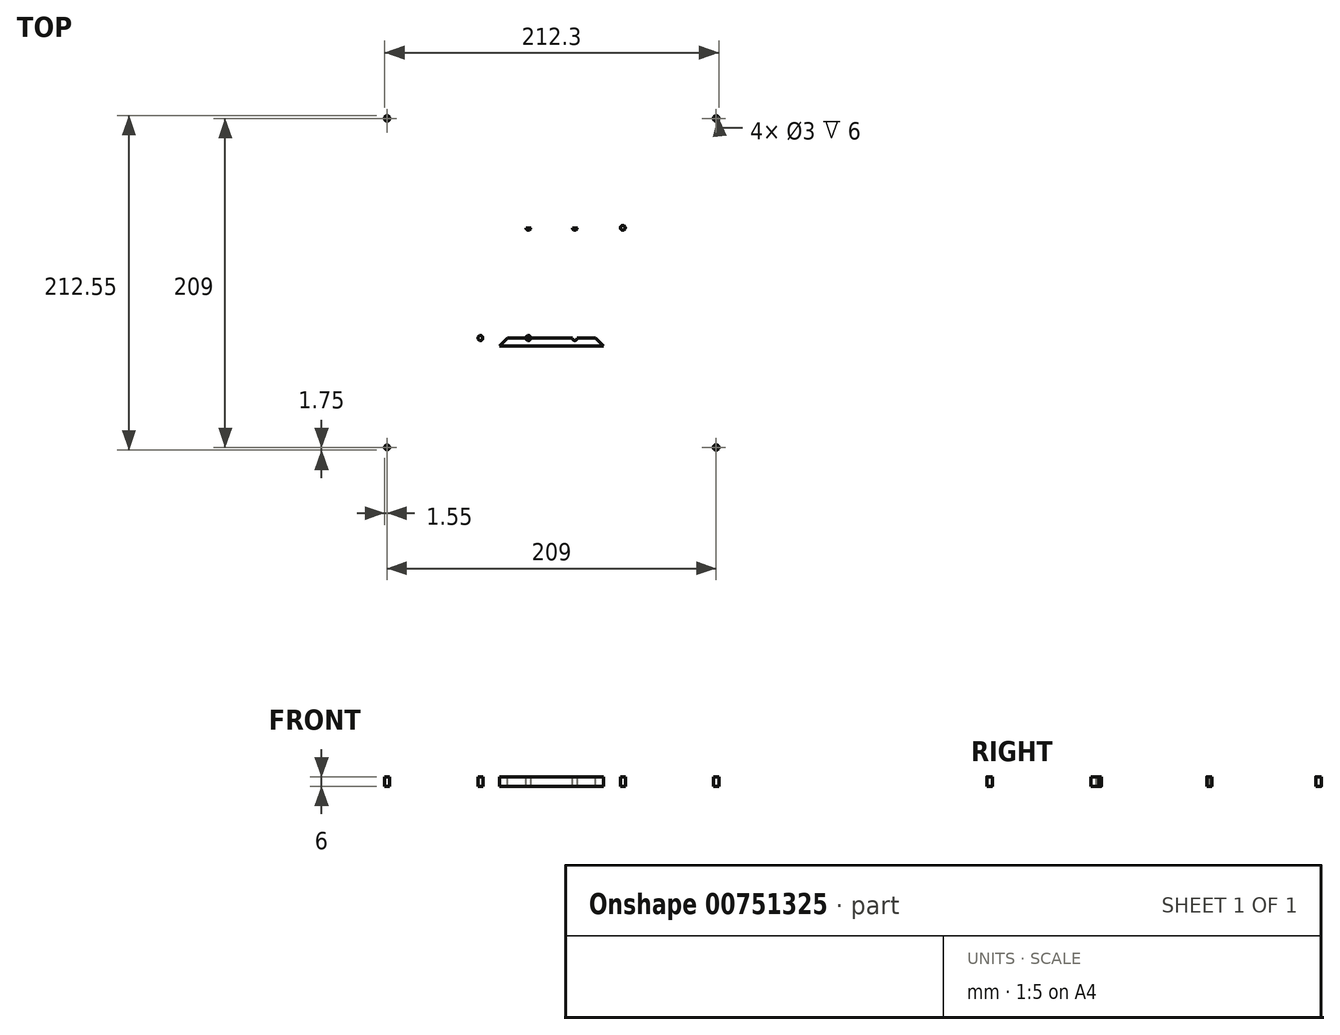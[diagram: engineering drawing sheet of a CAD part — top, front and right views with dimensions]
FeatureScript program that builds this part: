
annotation { "Feature Type Name" : "Feature", "Feature Type Description" : "" }
export const myFeature = defineFeature(function(context is Context, id is Id, definition is map)
    precondition{}
    {
        {
            var Q0;
            Q0=qCreatedBy(makeId("Top.planeOp"),FACE);
            var sketch = newSketch(context, id + "F0", { "sketchPlane" : qUnion([Q0])});
            skLineSegment(sketch, "E0", {"start": v(-180, -185) * mm, "end": v(-185, -180.2) * mm});
            skLineSegment(sketch, "E1", {"start": v(-185, -180.2) * mm, "end": v(-185, 180) * mm});
            skLineSegment(sketch, "E2", {"start": v(-185, 180) * mm, "end": v(-180, 185) * mm});
            skLineSegment(sketch, "E3", {"start": v(-180, 185) * mm, "end": v(180, 185) * mm});
            skLineSegment(sketch, "E4", {"start": v(180, 185) * mm, "end": v(185, 180) * mm});
            skLineSegment(sketch, "E5", {"start": v(185, 180) * mm, "end": v(185, -180) * mm});
            skLineSegment(sketch, "E6", {"start": v(185, -180) * mm, "end": v(180, -185) * mm});
            skLineSegment(sketch, "E7", {"start": v(180, -185) * mm, "end": v(160, -185) * mm});
            skLineSegment(sketch, "E8", {"start": v(160, -185) * mm, "end": v(158, -183) * mm});
            skLineSegment(sketch, "E9", {"start": v(144, -183) * mm, "end": v(-144, -183) * mm});
            skLineSegment(sketch, "E10", {"start": v(-158, -183) * mm, "end": v(-160, -185) * mm});
            skLineSegment(sketch, "E11", {"start": v(-160, -185) * mm, "end": v(-180, -185) * mm});
            skArc(sketch, "E12", {"start": v(-90, -165) * mm, "mid": v(-85, -170) * mm, "end": v(-80, -165) * mm});
            skLineSegment(sketch, "E13", {"start": v(-90, -165) * mm, "end": v(-90, -150) * mm});
            skLineSegment(sketch, "E14", {"start": v(-90, -150) * mm, "end": v(-105, -135) * mm});
            skLineSegment(sketch, "E15", {"start": v(-105, -135) * mm, "end": v(-125, -135) * mm});
            skLineSegment(sketch, "E16", {"start": v(-125, -135) * mm, "end": v(-130, -130) * mm});
            skLineSegment(sketch, "E17", {"start": v(-130, -130) * mm, "end": v(-130, 140) * mm});
            skLineSegment(sketch, "E18", {"start": v(-130, 140) * mm, "end": v(-125, 145) * mm});
            skLineSegment(sketch, "E19", {"start": v(-125, 145) * mm, "end": v(125, 145) * mm});
            skLineSegment(sketch, "E20", {"start": v(125, 145) * mm, "end": v(130, 140) * mm});
            skLineSegment(sketch, "E21", {"start": v(130, 140) * mm, "end": v(130, -130) * mm});
            skLineSegment(sketch, "E22", {"start": v(130, -130) * mm, "end": v(125, -135) * mm});
            skLineSegment(sketch, "E23", {"start": v(-80, -165) * mm, "end": v(-80, -150) * mm});
            skLineSegment(sketch, "E24", {"start": v(-80, -150) * mm, "end": v(-75, -145) * mm});
            skArc(sketch, "E25", {"start": v(80, -165) * mm, "mid": v(85, -170) * mm, "end": v(90, -165) * mm});
            skLineSegment(sketch, "E26", {"start": v(125, -135) * mm, "end": v(105, -135) * mm});
            skLineSegment(sketch, "E27", {"start": v(106, -134) * mm, "end": v(90, -150) * mm});
            skLineSegment(sketch, "E28", {"start": v(90, -150) * mm, "end": v(90, -165) * mm});
            skLineSegment(sketch, "E29", {"start": v(80, -165) * mm, "end": v(80, -150) * mm});
            skLineSegment(sketch, "E30", {"start": v(80, -150) * mm, "end": v(75, -145) * mm});
            skLineSegment(sketch, "E31", {"start": v(-5, -170) * mm, "end": v(5, -170) * mm});
            skLineSegment(sketch, "E32", {"start": v(5, -170) * mm, "end": v(30, -145) * mm});
            skLineSegment(sketch, "E33", {"start": v(-5, -170) * mm, "end": v(-30, -145) * mm});
            skLineSegment(sketch, "E34", {"start": v(-75, -145) * mm, "end": v(-30, -145) * mm});
            skLineSegment(sketch, "E35", {"start": v(30, -145) * mm, "end": v(75, -145) * mm});
            skLineSegment(sketch, "E36", {"start": v(-120, 140) * mm, "end": v(-122, 140) * mm});
            skLineSegment(sketch, "E37", {"start": v(-122, 140) * mm, "end": v(-125, 137) * mm});
            skLineSegment(sketch, "E38", {"start": v(-125, 137) * mm, "end": v(-125, 135) * mm});
            skLineSegment(sketch, "E39", {"start": v(-125, 135) * mm, "end": v(-125, 133) * mm});
            skLineSegment(sketch, "E40", {"start": v(-125, 133) * mm, "end": v(-105, 113) * mm});
            skLineSegment(sketch, "E41", {"start": v(-105, 113) * mm, "end": v(-105, 93) * mm});
            skLineSegment(sketch, "E42", {"start": v(-105, 93) * mm, "end": v(-115, 83) * mm});
            skLineSegment(sketch, "E43", {"start": v(-115, -23) * mm, "end": v(-105, -33) * mm});
            skLineSegment(sketch, "E44", {"start": v(-125, -73) * mm, "end": v(-105, -53) * mm});
            skLineSegment(sketch, "E45", {"start": v(-105, -53) * mm, "end": v(-105, -33) * mm});
            skLineSegment(sketch, "E46", {"start": v(-125, -73) * mm, "end": v(-125, -77) * mm});
            skLineSegment(sketch, "E47", {"start": v(-125, -77) * mm, "end": v(-122, -80) * mm});
            skLineSegment(sketch, "E48", {"start": v(-122, -80) * mm, "end": v(-120, -80) * mm});
            skLineSegment(sketch, "E49", {"start": v(90, -80) * mm, "end": v(92, -80) * mm});
            skLineSegment(sketch, "E50", {"start": v(92, -80) * mm, "end": v(95, -77) * mm});
            skLineSegment(sketch, "E51", {"start": v(95, 136) * mm, "end": v(95, 137) * mm});
            skLineSegment(sketch, "E52", {"start": v(95, 137) * mm, "end": v(92, 140) * mm});
            skLineSegment(sketch, "E53", {"start": v(95, 133) * mm, "end": v(55, 93) * mm});
            skLineSegment(sketch, "E54", {"start": v(85, 43) * mm, "end": v(75, 53) * mm});
            skLineSegment(sketch, "E55", {"start": v(75, 53) * mm, "end": v(55, 73) * mm});
            skLineSegment(sketch, "E56", {"start": v(55, 73) * mm, "end": v(55, 93) * mm});
            skLineSegment(sketch, "E57", {"start": v(85, 17) * mm, "end": v(75, 7) * mm});
            skLineSegment(sketch, "E58", {"start": v(75, 7) * mm, "end": v(55, -13) * mm});
            skLineSegment(sketch, "E59", {"start": v(95, -73) * mm, "end": v(75, -53) * mm});
            skLineSegment(sketch, "E60", {"start": v(75, -53) * mm, "end": v(55, -33) * mm});
            skLineSegment(sketch, "E61", {"start": v(55, -33) * mm, "end": v(55, -13) * mm});
            skLineSegment(sketch, "E62", {"start": v(88, 140) * mm, "end": v(65, 117) * mm});
            skLineSegment(sketch, "E63", {"start": v(25, 77) * mm, "end": v(23, 75) * mm});
            skLineSegment(sketch, "E64", {"start": v(23, 75) * mm, "end": v(13, 65) * mm});
            skLineSegment(sketch, "E65", {"start": v(13, 65) * mm, "end": v(-43, 65) * mm});
            skLineSegment(sketch, "E66", {"start": v(88, -80) * mm, "end": v(63, -55) * mm});
            skLineSegment(sketch, "E67", {"start": v(13, -5) * mm, "end": v(-43, -5) * mm});
            skLineSegment(sketch, "E68", {"start": v(-93, 115) * mm, "end": v(63, 115) * mm});
            skLineSegment(sketch, "E69", {"start": v(-93, -55) * mm, "end": v(63, -55) * mm});
            skLineSegment(sketch, "E70", {"start": v(-115, 45) * mm, "end": v(-105, 35) * mm});
            skLineSegment(sketch, "E71", {"start": v(-105, 35) * mm, "end": v(-105, 25) * mm});
            skLineSegment(sketch, "E72", {"start": v(-105, 25) * mm, "end": v(-115, 15) * mm});
            skLineSegment(sketch, "E73", {"start": v(-95, 35) * mm, "end": v(-75, 55) * mm});
            skLineSegment(sketch, "E74", {"start": v(-75, 55) * mm, "end": v(-55, 55) * mm});
            skLineSegment(sketch, "E75", {"start": v(-55, 55) * mm, "end": v(-35, 35) * mm});
            skLineSegment(sketch, "E76", {"start": v(-35, 35) * mm, "end": v(-35, 25) * mm});
            skLineSegment(sketch, "E77", {"start": v(-35, 25) * mm, "end": v(-55, 5) * mm});
            skLineSegment(sketch, "E78", {"start": v(-55, 5) * mm, "end": v(-75, 5) * mm});
            skLineSegment(sketch, "E79", {"start": v(-75, 5) * mm, "end": v(-95, 25) * mm});
            skLineSegment(sketch, "E80", {"start": v(-95, 25) * mm, "end": v(-95, 35) * mm});
            skLineSegment(sketch, "E81", {"start": v(35, 55) * mm, "end": v(55, 35) * mm});
            skLineSegment(sketch, "E82", {"start": v(55, 35) * mm, "end": v(55, 25) * mm});
            skLineSegment(sketch, "E83", {"start": v(55, 25) * mm, "end": v(35, 5) * mm});
            skLineSegment(sketch, "E84", {"start": v(35, 5) * mm, "end": v(25, 5) * mm});
            skLineSegment(sketch, "E85", {"start": v(25, 5) * mm, "end": v(5, 25) * mm});
            skLineSegment(sketch, "E86", {"start": v(5, 25) * mm, "end": v(5, 35) * mm});
            skLineSegment(sketch, "E87", {"start": v(5, 35) * mm, "end": v(25, 55) * mm});
            skLineSegment(sketch, "E88", {"start": v(25, 55) * mm, "end": v(35, 55) * mm});
            skLineSegment(sketch, "E89", {"start": v(-120, 140) * mm, "end": v(-118, 140) * mm});
            skLineSegment(sketch, "E90", {"start": v(92, 140) * mm, "end": v(88, 140) * mm});
            skLineSegment(sketch, "E91", {"start": v(95, 136) * mm, "end": v(95, 133) * mm});
            skLineSegment(sketch, "E92", {"start": v(95, -73) * mm, "end": v(95, -77) * mm});
            skLineSegment(sketch, "E93", {"start": v(88, -80) * mm, "end": v(90, -80) * mm});
            skLineSegment(sketch, "E94", {"start": v(-118, -80) * mm, "end": v(-120, -80) * mm});
            skLineSegment(sketch, "E95", {"start": v(-83, 105) * mm, "end": v(53, 105) * mm});
            skLineSegment(sketch, "E96", {"start": v(65, 117) * mm, "end": v(63, 115) * mm});
            skLineSegment(sketch, "E97", {"start": v(53, 105) * mm, "end": v(25, 77) * mm});
            skLineSegment(sketch, "E98", {"start": v(-118, 140) * mm, "end": v(-93, 115) * mm});
            skLineSegment(sketch, "E99", {"start": v(-83, 105) * mm, "end": v(-43, 65) * mm});
            skLineSegment(sketch, "E100", {"start": v(53, -45) * mm, "end": v(-83, -45) * mm});
            skLineSegment(sketch, "E101", {"start": v(-118, -80) * mm, "end": v(-93, -55) * mm});
            skLineSegment(sketch, "E102", {"start": v(-43, -5) * mm, "end": v(-83, -45) * mm});
            skLineSegment(sketch, "E103", {"start": v(13, -5) * mm, "end": v(53, -45) * mm});
            skLineSegment(sketch, "E104", {"start": v(-127.97, 156.16) * mm, "end": v(-127.9, 173.41) * mm});
            skLineSegment(sketch, "E105", {"start": v(-127.9, 173.41) * mm, "end": v(-120.91, 173.41) * mm});
            skLineSegment(sketch, "E106", {"start": v(-120.91, 173.41) * mm, "end": v(-118.76, 172.76) * mm});
            skLineSegment(sketch, "E107", {"start": v(-118.76, 172.76) * mm, "end": v(-117.71, 171.78) * mm});
            skLineSegment(sketch, "E108", {"start": v(-117.71, 171.78) * mm, "end": v(-117, 170.47) * mm});
            skLineSegment(sketch, "E109", {"start": v(-117, 170.47) * mm, "end": v(-116.67, 168.7) * mm});
            skLineSegment(sketch, "E110", {"start": v(-116.67, 168.7) * mm, "end": v(-117, 167) * mm});
            skLineSegment(sketch, "E111", {"start": v(-117, 167) * mm, "end": v(-117.84, 165.57) * mm});
            skLineSegment(sketch, "E112", {"start": v(-117.84, 165.57) * mm, "end": v(-119.02, 164.85) * mm});
            skLineSegment(sketch, "E113", {"start": v(-119.02, 164.85) * mm, "end": v(-120.2, 164.52) * mm});
            skLineSegment(sketch, "E114", {"start": v(-120.2, 164.52) * mm, "end": v(-121.63, 164.33) * mm});
            skLineSegment(sketch, "E115", {"start": v(-121.63, 164.33) * mm, "end": v(-123.4, 164.33) * mm});
            skLineSegment(sketch, "E116", {"start": v(-109.35, 156.03) * mm, "end": v(-109.41, 173.41) * mm});
            skLineSegment(sketch, "E117", {"start": v(-109.41, 173.41) * mm, "end": v(-102.62, 173.48) * mm});
            skLineSegment(sketch, "E118", {"start": v(-102.62, 173.48) * mm, "end": v(-100, 172.82) * mm});
            skLineSegment(sketch, "E119", {"start": v(-100, 172.82) * mm, "end": v(-98.83, 171.45) * mm});
            skLineSegment(sketch, "E120", {"start": v(-98.83, 171.45) * mm, "end": v(-98.24, 170.14) * mm});
            skLineSegment(sketch, "E121", {"start": v(-98.24, 170.14) * mm, "end": v(-98.05, 169.03) * mm});
            skLineSegment(sketch, "E122", {"start": v(-98.05, 169.03) * mm, "end": v(-98.18, 167.33) * mm});
            skLineSegment(sketch, "E123", {"start": v(-98.18, 167.33) * mm, "end": v(-98.76, 166.22) * mm});
            skLineSegment(sketch, "E124", {"start": v(-98.76, 166.22) * mm, "end": v(-99.68, 165.3) * mm});
            skLineSegment(sketch, "E125", {"start": v(-99.68, 165.3) * mm, "end": v(-100.53, 164.79) * mm});
            skLineSegment(sketch, "E126", {"start": v(-100.53, 164.79) * mm, "end": v(-102.03, 164.4) * mm});
            skLineSegment(sketch, "E127", {"start": v(-102.03, 164.4) * mm, "end": v(-103.47, 164.26) * mm});
            skLineSegment(sketch, "E128", {"start": v(-103.47, 164.26) * mm, "end": v(-104.78, 164.26) * mm});
            skLineSegment(sketch, "E129", {"start": v(-104.78, 164.26) * mm, "end": v(-102.88, 164.33) * mm});
            skLineSegment(sketch, "E130", {"start": v(-102.88, 164.33) * mm, "end": v(-101.97, 163.8) * mm});
            skLineSegment(sketch, "E131", {"start": v(-101.97, 163.8) * mm, "end": v(-100.92, 162.43) * mm});
            skLineSegment(sketch, "E132", {"start": v(-100.92, 162.43) * mm, "end": v(-96.48, 156.1) * mm});
            skLineSegment(sketch, "E133", {"start": v(-89.23, 173.41) * mm, "end": v(-89.3, 162.83) * mm});
            skLineSegment(sketch, "E134", {"start": v(-89.3, 162.83) * mm, "end": v(-89.03, 160.74) * mm});
            skLineSegment(sketch, "E135", {"start": v(-89.03, 160.74) * mm, "end": v(-88.5, 159.23) * mm});
            skLineSegment(sketch, "E136", {"start": v(-88.5, 159.23) * mm, "end": v(-87.79, 158.19) * mm});
            skLineSegment(sketch, "E137", {"start": v(-87.79, 158.19) * mm, "end": v(-86.79, 156.96) * mm});
            skLineSegment(sketch, "E138", {"start": v(-86.79, 156.96) * mm, "end": v(-85.16, 156.43) * mm});
            skLineSegment(sketch, "E139", {"start": v(-85.16, 156.43) * mm, "end": v(-83.35, 156.1) * mm});
            skLineSegment(sketch, "E140", {"start": v(-83.35, 156.1) * mm, "end": v(-81, 156.36) * mm});
            skLineSegment(sketch, "E141", {"start": v(-81, 156.36) * mm, "end": v(-78.97, 157.4) * mm});
            skLineSegment(sketch, "E142", {"start": v(-78.97, 157.4) * mm, "end": v(-77.86, 159.23) * mm});
            skLineSegment(sketch, "E143", {"start": v(-77.86, 159.23) * mm, "end": v(-77.4, 161.72) * mm});
            skLineSegment(sketch, "E144", {"start": v(-77.4, 161.72) * mm, "end": v(-77.4, 164.2) * mm});
            skLineSegment(sketch, "E145", {"start": v(-77.4, 164.2) * mm, "end": v(-77.47, 173.48) * mm});
            skLineSegment(sketch, "E146", {"start": v(-51.97, 156.03) * mm, "end": v(-44.98, 173.54) * mm});
            skLineSegment(sketch, "E147", {"start": v(-44.98, 173.54) * mm, "end": v(-43.87, 173.54) * mm});
            skLineSegment(sketch, "E148", {"start": v(-43.87, 173.54) * mm, "end": v(-37.01, 156.03) * mm});
            skLineSegment(sketch, "E149", {"start": v(-39.04, 161.2) * mm, "end": v(-49.89, 161.2) * mm});
            skLineSegment(sketch, "E150", {"start": v(-69.88, 160.44) * mm, "end": v(-68.77, 158.48) * mm});
            skLineSegment(sketch, "E151", {"start": v(-68.77, 158.48) * mm, "end": v(-66.35, 156.85) * mm});
            skLineSegment(sketch, "E152", {"start": v(-66.35, 156.85) * mm, "end": v(-64, 156.2) * mm});
            skLineSegment(sketch, "E153", {"start": v(-64, 156.2) * mm, "end": v(-60.54, 156.72) * mm});
            skLineSegment(sketch, "E154", {"start": v(-60.54, 156.72) * mm, "end": v(-58.9, 158.03) * mm});
            skLineSegment(sketch, "E155", {"start": v(-58.9, 158.03) * mm, "end": v(-57.73, 160.12) * mm});
            skLineSegment(sketch, "E156", {"start": v(-57.73, 160.12) * mm, "end": v(-57.73, 161.36) * mm});
            skLineSegment(sketch, "E157", {"start": v(-57.73, 161.36) * mm, "end": v(-58.05, 162.47) * mm});
            skLineSegment(sketch, "E158", {"start": v(-58.05, 162.47) * mm, "end": v(-59.23, 163.78) * mm});
            skLineSegment(sketch, "E159", {"start": v(-59.23, 163.78) * mm, "end": v(-60.4, 164.3) * mm});
            skLineSegment(sketch, "E160", {"start": v(-60.4, 164.3) * mm, "end": v(-66.22, 166.06) * mm});
            skLineSegment(sketch, "E161", {"start": v(-66.22, 166.06) * mm, "end": v(-67.92, 167.17) * mm});
            skLineSegment(sketch, "E162", {"start": v(-67.92, 167.17) * mm, "end": v(-68.97, 168.42) * mm});
            skLineSegment(sketch, "E163", {"start": v(-68.97, 168.42) * mm, "end": v(-69.1, 169.6) * mm});
            skLineSegment(sketch, "E164", {"start": v(-69.1, 169.6) * mm, "end": v(-68.84, 171.36) * mm});
            skLineSegment(sketch, "E165", {"start": v(-68.84, 171.36) * mm, "end": v(-67.6, 172.66) * mm});
            skLineSegment(sketch, "E166", {"start": v(-67.6, 172.66) * mm, "end": v(-65.5, 173.45) * mm});
            skLineSegment(sketch, "E167", {"start": v(-65.5, 173.45) * mm, "end": v(-62.89, 173.58) * mm});
            skLineSegment(sketch, "E168", {"start": v(-62.89, 173.58) * mm, "end": v(-60.15, 172.86) * mm});
            skLineSegment(sketch, "E169", {"start": v(-60.15, 172.86) * mm, "end": v(-59.03, 171.81) * mm});
            skLineSegment(sketch, "E170", {"start": v(-59.03, 171.81) * mm, "end": v(-58.58, 170.57) * mm});
            skLineSegment(sketch, "E171", {"start": v(-123.4, 164.33) * mm, "end": v(-127.94, 164.43) * mm});
            skLineSegment(sketch, "E172", {"start": v(-104.78, 164.26) * mm, "end": v(-109.38, 164.23) * mm});
            skLineSegment(sketch, "E173", {"start": v(-115, 83) * mm, "end": v(-115, 45) * mm});
            skLineSegment(sketch, "E174", {"start": v(-115, 15) * mm, "end": v(-115, -23) * mm});
            skLineSegment(sketch, "E175", {"start": v(85, 43) * mm, "end": v(85, 17) * mm});
            skCircle(sketch, "E176", {"center": v(-181.26, -3.72) * mm, "radius": 1.5 * mm});
            skCircle(sketch, "E177", {"center": v(-133, -10.07) * mm, "radius": 1.5 * mm});
            skCircle(sketch, "E178", {"center": v(-133, -85) * mm, "radius": 1.5 * mm});
            skCircle(sketch, "E179", {"center": v(-181.26, -85) * mm, "radius": 1.5 * mm});
            skCircle(sketch, "E180", {"center": v(-110, 65) * mm, "radius": 1.5 * mm});
            skCircle(sketch, "E181", {"center": v(-90, 65) * mm, "radius": 1.5 * mm});
            skCircle(sketch, "E182", {"center": v(-110, -5) * mm, "radius": 1.5 * mm});
            skCircle(sketch, "E183", {"center": v(-90, -5) * mm, "radius": 1.5 * mm});
            skCircle(sketch, "E184", {"center": v(80, 30) * mm, "radius": 1.5 * mm});
            skCircle(sketch, "E185", {"center": v(60, 30) * mm, "radius": 1.5 * mm});
            skCircle(sketch, "E186", {"center": v(-119.5, 134.5) * mm, "radius": 1.5 * mm});
            skCircle(sketch, "E187", {"center": v(89.5, -74.5) * mm, "radius": 1.5 * mm});
            skCircle(sketch, "E188", {"center": v(89.5, 134.5) * mm, "radius": 1.5 * mm});
            skCircle(sketch, "E189", {"center": v(-119.5, -74.5) * mm, "radius": 1.5 * mm});
            skLineSegment(sketch, "E190", {"start": v(158, -183) * mm, "end": v(154, -179) * mm});
            skLineSegment(sketch, "E191", {"start": v(154, -179) * mm, "end": v(148, -179) * mm});
            skLineSegment(sketch, "E192", {"start": v(148, -179) * mm, "end": v(144, -183) * mm});
            skLineSegment(sketch, "E193", {"start": v(-158, -183) * mm, "end": v(-154, -179) * mm});
            skLineSegment(sketch, "E194", {"start": v(-154, -179) * mm, "end": v(-148, -179) * mm});
            skLineSegment(sketch, "E195", {"start": v(-148, -179) * mm, "end": v(-144, -183) * mm});
            skCircle(sketch, "E196", {"center": v(-135, -179) * mm, "radius": 1.5 * mm});
            skCircle(sketch, "E197", {"center": v(135, -179) * mm, "radius": 1.5 * mm});
            skCircle(sketch, "E198", {"center": v(45, -179) * mm, "radius": 1.5 * mm});
            skCircle(sketch, "E199", {"center": v(-45, -179) * mm, "radius": 1.5 * mm});
            skLineSegment(sketch, "E200", {"start": v(-105, -16) * mm, "end": v(-105, 7) * mm});
            skArc(sketch, "E201", {"start": v(-101, 11) * mm, "mid": v(-103.83, 9.83) * mm, "end": v(-105, 7) * mm});
            skLineSegment(sketch, "E202", {"start": v(-101, 11) * mm, "end": v(-99, 11) * mm});
            skArc(sketch, "E203", {"start": v(-95, 7) * mm, "mid": v(-96.17, 9.83) * mm, "end": v(-99, 11) * mm});
            skLineSegment(sketch, "E204", {"start": v(-95, 7) * mm, "end": v(-95, -16) * mm});
            skArc(sketch, "E205", {"start": v(-105, -16) * mm, "mid": v(-103.83, -18.83) * mm, "end": v(-101, -20) * mm});
            skLineSegment(sketch, "E206", {"start": v(-99, -20) * mm, "end": v(-101, -20) * mm});
            skArc(sketch, "E207", {"start": v(-99, -20) * mm, "mid": v(-96.17, -18.83) * mm, "end": v(-95, -16) * mm});
            skCircle(sketch, "E208", {"center": v(-175, -145) * mm, "radius": 1.5 * mm});
            skCircle(sketch, "E209", {"center": v(-155, -145) * mm, "radius": 1.5 * mm});
            skCircle(sketch, "E210", {"center": v(-165, -165) * mm, "radius": 1.5 * mm});
            skCircle(sketch, "E211", {"center": v(165, -165) * mm, "radius": 1.5 * mm});
            skCircle(sketch, "E212", {"center": v(155, -145) * mm, "radius": 1.5 * mm});
            skCircle(sketch, "E213", {"center": v(175, -145) * mm, "radius": 1.5 * mm});
            skCircle(sketch, "E214", {"center": v(175, 175) * mm, "radius": 1.5 * mm});
            skCircle(sketch, "E215", {"center": v(155, 175) * mm, "radius": 1.5 * mm});
            skCircle(sketch, "E216", {"center": v(-175, 175) * mm, "radius": 1.5 * mm});
            skCircle(sketch, "E217", {"center": v(-155, 175) * mm, "radius": 1.5 * mm});
            skCircle(sketch, "E218", {"center": v(-15, 50) * mm, "radius": 1.5 * mm, "construction": true});
            skArc(sketch, "E219", {"start": v(-99, 50) * mm, "mid": v(-96.17, 51.18) * mm, "end": v(-95, 54) * mm});
            skLineSegment(sketch, "E220", {"start": v(-105, 54) * mm, "end": v(-105, 77) * mm});
            skArc(sketch, "E221", {"start": v(-101, 81) * mm, "mid": v(-103.83, 79.84) * mm, "end": v(-105, 77) * mm});
            skLineSegment(sketch, "E222", {"start": v(-101, 81) * mm, "end": v(-99, 81) * mm});
            skArc(sketch, "E223", {"start": v(-95, 77) * mm, "mid": v(-96.17, 79.84) * mm, "end": v(-99, 81) * mm});
            skLineSegment(sketch, "E224", {"start": v(-95, 77) * mm, "end": v(-95, 54) * mm});
            skArc(sketch, "E225", {"start": v(-105, 54) * mm, "mid": v(-103.83, 51.18) * mm, "end": v(-101, 50) * mm});
            skLineSegment(sketch, "E226", {"start": v(-99, 50) * mm, "end": v(-101, 50) * mm});
            skArc(sketch, "E227", {"start": v(71, 13.86) * mm, "mid": v(73.83, 15.03) * mm, "end": v(75, 17.86) * mm});
            skLineSegment(sketch, "E228", {"start": v(65, 17.86) * mm, "end": v(65, 40.86) * mm});
            skArc(sketch, "E229", {"start": v(69, 44.86) * mm, "mid": v(66.17, 43.7) * mm, "end": v(65, 40.86) * mm});
            skLineSegment(sketch, "E230", {"start": v(69, 44.86) * mm, "end": v(71, 44.86) * mm});
            skArc(sketch, "E231", {"start": v(75, 40.86) * mm, "mid": v(73.83, 43.7) * mm, "end": v(71, 44.86) * mm});
            skLineSegment(sketch, "E232", {"start": v(75, 40.86) * mm, "end": v(75, 17.86) * mm});
            skArc(sketch, "E233", {"start": v(65, 17.86) * mm, "mid": v(66.17, 15.03) * mm, "end": v(69, 13.86) * mm});
            skLineSegment(sketch, "E234", {"start": v(71, 13.86) * mm, "end": v(69, 13.86) * mm});
            skCircle(sketch, "E235", {"center": v(-137.05, -117.03) * mm, "radius": 1.5 * mm});
            skCircle(sketch, "E236", {"center": v(-180.05, -23.03) * mm, "radius": 1.5 * mm});
            skCircle(sketch, "E237", {"center": v(-137.05, -23.03) * mm, "radius": 1.5 * mm});
            skCircle(sketch, "E238", {"center": v(-180.05, 84.47) * mm, "radius": 1.5 * mm});
            skCircle(sketch, "E239", {"center": v(-137.05, 84.47) * mm, "radius": 1.5 * mm});
            skCircle(sketch, "E240", {"center": v(-180.08, -117) * mm, "radius": 1.5 * mm});
            skCircle(sketch, "E241", {"center": v(-180.08, 84.5) * mm, "radius": 1.5 * mm});
            skCircle(sketch, "E242", {"center": v(-137.08, 84.5) * mm, "radius": 1.5 * mm});
            skSolve(sketch);
        }
        {
            var Q0;
            Q0=makeQuery(id+"F0.imprint","IMPRINT",FACE,{"disambiguationData":[TD([[makeQuery(id+"F0.imprint","IMPRINT",EDGE,{"derivedFrom":sQuery(id+"F0.wireOp",EDGE,"E36")}),1.0]])]});
            extrude(context, id + "F1", {"entities" : qUnion([Q0]), "depth" : 6 * mm, "offsetDistance" : 25 * mm});
        }
        {
            var Q0;
            Q0=makeQuery(id+"F1.opExtrude","CAP_FACE",FACE,{"disambiguationData":[OSD([sQuery(id+"F0.wireOp",EDGE,"E36"),sQuery(id+"F0.wireOp",EDGE,"E37"),sQuery(id+"F0.wireOp",EDGE,"E38"),sQuery(id+"F0.wireOp",EDGE,"E39"),sQuery(id+"F0.wireOp",EDGE,"E40"),sQuery(id+"F0.wireOp",EDGE,"E41"),sQuery(id+"F0.wireOp",EDGE,"E42"),sQuery(id+"F0.wireOp",EDGE,"E43"),sQuery(id+"F0.wireOp",EDGE,"E44"),sQuery(id+"F0.wireOp",EDGE,"E45"),sQuery(id+"F0.wireOp",EDGE,"E46"),sQuery(id+"F0.wireOp",EDGE,"E47"),sQuery(id+"F0.wireOp",EDGE,"E48"),sQuery(id+"F0.wireOp",EDGE,"E49"),sQuery(id+"F0.wireOp",EDGE,"E50"),sQuery(id+"F0.wireOp",EDGE,"E51"),sQuery(id+"F0.wireOp",EDGE,"E52"),sQuery(id+"F0.wireOp",EDGE,"E53"),sQuery(id+"F0.wireOp",EDGE,"E54"),sQuery(id+"F0.wireOp",EDGE,"E55"),sQuery(id+"F0.wireOp",EDGE,"E56"),sQuery(id+"F0.wireOp",EDGE,"E57"),sQuery(id+"F0.wireOp",EDGE,"E58"),sQuery(id+"F0.wireOp",EDGE,"E59"),sQuery(id+"F0.wireOp",EDGE,"E60"),sQuery(id+"F0.wireOp",EDGE,"E61"),sQuery(id+"F0.wireOp",EDGE,"E62"),sQuery(id+"F0.wireOp",EDGE,"E63"),sQuery(id+"F0.wireOp",EDGE,"E64"),sQuery(id+"F0.wireOp",EDGE,"E65"),sQuery(id+"F0.wireOp",EDGE,"E66"),sQuery(id+"F0.wireOp",EDGE,"E67"),sQuery(id+"F0.wireOp",EDGE,"E68"),sQuery(id+"F0.wireOp",EDGE,"E69"),sQuery(id+"F0.wireOp",EDGE,"E70"),sQuery(id+"F0.wireOp",EDGE,"E71"),sQuery(id+"F0.wireOp",EDGE,"E72"),sQuery(id+"F0.wireOp",EDGE,"E73"),sQuery(id+"F0.wireOp",EDGE,"E74"),sQuery(id+"F0.wireOp",EDGE,"E75"),sQuery(id+"F0.wireOp",EDGE,"E76"),sQuery(id+"F0.wireOp",EDGE,"E77"),sQuery(id+"F0.wireOp",EDGE,"E78"),sQuery(id+"F0.wireOp",EDGE,"E79"),sQuery(id+"F0.wireOp",EDGE,"E80"),sQuery(id+"F0.wireOp",EDGE,"E81"),sQuery(id+"F0.wireOp",EDGE,"E82"),sQuery(id+"F0.wireOp",EDGE,"E83"),sQuery(id+"F0.wireOp",EDGE,"E84"),sQuery(id+"F0.wireOp",EDGE,"E85"),sQuery(id+"F0.wireOp",EDGE,"E86"),sQuery(id+"F0.wireOp",EDGE,"E87"),sQuery(id+"F0.wireOp",EDGE,"E88"),sQuery(id+"F0.wireOp",EDGE,"E89"),sQuery(id+"F0.wireOp",EDGE,"E90"),sQuery(id+"F0.wireOp",EDGE,"E91"),sQuery(id+"F0.wireOp",EDGE,"E92"),sQuery(id+"F0.wireOp",EDGE,"E93"),sQuery(id+"F0.wireOp",EDGE,"E94"),sQuery(id+"F0.wireOp",EDGE,"E95"),sQuery(id+"F0.wireOp",EDGE,"E96"),sQuery(id+"F0.wireOp",EDGE,"E97"),sQuery(id+"F0.wireOp",EDGE,"E98"),sQuery(id+"F0.wireOp",EDGE,"E99"),sQuery(id+"F0.wireOp",EDGE,"E100"),sQuery(id+"F0.wireOp",EDGE,"E101"),sQuery(id+"F0.wireOp",EDGE,"E102"),sQuery(id+"F0.wireOp",EDGE,"E103"),sQuery(id+"F0.wireOp",EDGE,"E173"),sQuery(id+"F0.wireOp",EDGE,"E174"),sQuery(id+"F0.wireOp",EDGE,"E175"),sQuery(id+"F0.wireOp",EDGE,"E180"),sQuery(id+"F0.wireOp",EDGE,"E181"),sQuery(id+"F0.wireOp",EDGE,"E182"),sQuery(id+"F0.wireOp",EDGE,"E183"),sQuery(id+"F0.wireOp",EDGE,"E184"),sQuery(id+"F0.wireOp",EDGE,"E185"),sQuery(id+"F0.wireOp",EDGE,"E186"),sQuery(id+"F0.wireOp",EDGE,"E187"),sQuery(id+"F0.wireOp",EDGE,"E188"),sQuery(id+"F0.wireOp",EDGE,"E189"),sQuery(id+"F0.wireOp",EDGE,"E200"),sQuery(id+"F0.wireOp",EDGE,"E201"),sQuery(id+"F0.wireOp",EDGE,"E202"),sQuery(id+"F0.wireOp",EDGE,"E203"),sQuery(id+"F0.wireOp",EDGE,"E204"),sQuery(id+"F0.wireOp",EDGE,"E205"),sQuery(id+"F0.wireOp",EDGE,"E206"),sQuery(id+"F0.wireOp",EDGE,"E207"),sQuery(id+"F0.wireOp",EDGE,"97428e1f-2df1-4eb4-ba85-a1d425946b56"),sQuery(id+"F0.wireOp",EDGE,"E218"),sQuery(id+"F0.wireOp",EDGE,"E219"),sQuery(id+"F0.wireOp",EDGE,"E220"),sQuery(id+"F0.wireOp",EDGE,"E221"),sQuery(id+"F0.wireOp",EDGE,"E222"),sQuery(id+"F0.wireOp",EDGE,"E223"),sQuery(id+"F0.wireOp",EDGE,"E224"),sQuery(id+"F0.wireOp",EDGE,"E225"),sQuery(id+"F0.wireOp",EDGE,"E226"),sQuery(id+"F0.wireOp",EDGE,"E227"),sQuery(id+"F0.wireOp",EDGE,"E228"),sQuery(id+"F0.wireOp",EDGE,"E229"),sQuery(id+"F0.wireOp",EDGE,"E230"),sQuery(id+"F0.wireOp",EDGE,"E231"),sQuery(id+"F0.wireOp",EDGE,"E232"),sQuery(id+"F0.wireOp",EDGE,"E233"),sQuery(id+"F0.wireOp",EDGE,"E234")])],"isStart":false});
            var sketch = newSketch(context, id + "F2", { "sketchPlane" : qUnion([Q0])});
            skCircle(sketch, "E243.0", {"center": v(-119.5, 134.5) * mm, "radius": 1.5 * mm, "construction": true});
            skCircle(sketch, "E244.0", {"center": v(89.5, 134.5) * mm, "radius": 1.5 * mm, "construction": true});
            skCircle(sketch, "E245.0", {"center": v(-119.5, -74.5) * mm, "radius": 1.5 * mm, "construction": true});
            skCircle(sketch, "E246.0", {"center": v(89.5, -74.5) * mm, "radius": 1.5 * mm, "construction": true});
            skLineSegment(sketch, "E247", {"start": v(-119.5, -74.5) * mm, "end": v(89.5, -74.5) * mm, "construction": true});
            skLineSegment(sketch, "E248", {"start": v(-119.5, 134.5) * mm, "end": v(89.5, 134.5) * mm, "construction": true});
            skLineSegment(sketch, "E249", {"start": v(-15, 134.5) * mm, "end": v(-15, -74.5) * mm, "construction": true});
            skCircle(sketch, "E250.0", {"center": v(-110, 65) * mm, "radius": 1.5 * mm, "construction": true});
            skCircle(sketch, "E251.0", {"center": v(-110, -5) * mm, "radius": 1.5 * mm, "construction": true});
            skLineSegment(sketch, "E252.bottom", {"start": v(15, 180) * mm, "end": v(-45, 180) * mm, "construction": true});
            skLineSegment(sketch, "E252.top", {"start": v(15, -120) * mm, "end": v(-45, -120) * mm, "construction": true});
            skLineSegment(sketch, "E252.left", {"start": v(15, 180) * mm, "end": v(15, -120) * mm, "construction": true});
            skLineSegment(sketch, "E252.right", {"start": v(-45, 180) * mm, "end": v(-45, -120) * mm, "construction": true});
            skPoint(sketch, "E252.middle", {"position": v(-15, 30) * mm});
            skLineSegment(sketch, "E253", {"start": v(-60.25, 65) * mm, "end": v(-29.75, 65) * mm, "construction": true});
            skCircle(sketch, "E254", {"center": v(-60.25, 65) * mm, "radius": 1.55 * mm});
            skCircle(sketch, "E255", {"center": v(-29.75, 65) * mm, "radius": 1.55 * mm});
            skLineSegment(sketch, "E256", {"start": v(-15, 30) * mm, "end": v(-183.13, 30) * mm, "construction": true});
            skCircle(sketch, "E257.MirrorC", {"center": v(-60.25, -5) * mm, "radius": 1.55 * mm});
            skCircle(sketch, "E258.MirrorC", {"center": v(-29.75, -5) * mm, "radius": 1.55 * mm});
            skCircle(sketch, "E259.MirrorC", {"center": v(30.25, 65) * mm, "radius": 1.55 * mm});
            skCircle(sketch, "E260.MirrorC", {"center": v(-0.25, 65) * mm, "radius": 1.55 * mm});
            skCircle(sketch, "E261.MirrorC", {"center": v(30.25, -5) * mm, "radius": 1.55 * mm});
            skCircle(sketch, "E262.MirrorC", {"center": v(-0.25, -5) * mm, "radius": 1.55 * mm});
            skLineSegment(sketch, "E263", {"start": v(-48, 70) * mm, "end": v(18, 70) * mm});
            skLineSegment(sketch, "E264", {"start": v(-48, 70) * mm, "end": v(-43, 65) * mm});
            skLineSegment(sketch, "E265", {"start": v(-43, 65) * mm, "end": v(13, 65) * mm});
            skLineSegment(sketch, "E266", {"start": v(13, 65) * mm, "end": v(18, 70) * mm});
            skLineSegment(sketch, "E267.MirrorCS", {"start": v(-48, -10) * mm, "end": v(-43, -5) * mm});
            skLineSegment(sketch, "E268.MirrorCS", {"start": v(-48, -10) * mm, "end": v(18, -10) * mm});
            skLineSegment(sketch, "E269.MirrorCS", {"start": v(13, -5) * mm, "end": v(18, -10) * mm});
            skLineSegment(sketch, "E270.MirrorCS", {"start": v(-43, -5) * mm, "end": v(13, -5) * mm});
            skCircle(sketch, "E271.0", {"center": v(-119.5, -74.5) * mm, "radius": 1.55 * mm});
            skLineSegment(sketch, "E272", {"start": v(-119.5, 134.75) * mm, "end": v(-119.5, 134.25) * mm});
            skArc(sketch, "E273.0.startCap", {"start": v(-121.05, 134.75) * mm, "mid": v(-119.5, 136.3) * mm, "end": v(-117.95, 134.75) * mm});
            skArc(sketch, "E273.0.endCap", {"start": v(-117.95, 134.25) * mm, "mid": v(-119.5, 132.7) * mm, "end": v(-121.05, 134.25) * mm});
            skLineSegment(sketch, "E273.0.left", {"start": v(-117.95, 134.75) * mm, "end": v(-117.95, 134.25) * mm});
            skLineSegment(sketch, "E273.0.right", {"start": v(-121.05, 134.75) * mm, "end": v(-121.05, 134.25) * mm});
            skCircle(sketch, "E274.0", {"center": v(89.5, 134.5) * mm, "radius": 1.75 * mm});
            skCircle(sketch, "E275.0", {"center": v(89.5, -74.5) * mm, "radius": 1.75 * mm});
            skPoint(sketch, "E276", {"position": v(-15, 50) * mm});
            skPoint(sketch, "E277", {"position": v(-15, 10) * mm});
            skCircle(sketch, "E278", {"center": v(-15, 50) * mm, "radius": 1.75 * mm});
            skCircle(sketch, "E279", {"center": v(-15, 10) * mm, "radius": 1.75 * mm});
            skSolve(sketch);
        }
        {
            var Q0;
            Q0=makeQuery(id+"F2.imprint","IMPRINT",FACE,{"disambiguationData":[TD([[makeQuery(id+"F2.imprint","IMPRINT",EDGE,{"derivedFrom":sQuery(id+"F2.wireOp",EDGE,"E263")}),-1.0]])]});
            var Q1;
            {var subQ4=sQuery(id+"F2.wireOp",EDGE,"E267.MirrorCS");Q1=makeQuery(id+"F2.imprint","IMPRINT",FACE,{"disambiguationData":[TD([[makeQuery(id+"F2.imprint","IMPRINT",EDGE,{"derivedFrom":subQ4}),1.0]])]});}
            var Q2;
            Q2=makeQuery(id+"F1.opExtrude","CAP_FACE",FACE,{"disambiguationData":[OSD([sQuery(id+"F0.wireOp",EDGE,"E36"),sQuery(id+"F0.wireOp",EDGE,"E37"),sQuery(id+"F0.wireOp",EDGE,"E38"),sQuery(id+"F0.wireOp",EDGE,"E39"),sQuery(id+"F0.wireOp",EDGE,"E40"),sQuery(id+"F0.wireOp",EDGE,"E41"),sQuery(id+"F0.wireOp",EDGE,"E42"),sQuery(id+"F0.wireOp",EDGE,"E43"),sQuery(id+"F0.wireOp",EDGE,"E44"),sQuery(id+"F0.wireOp",EDGE,"E45"),sQuery(id+"F0.wireOp",EDGE,"E46"),sQuery(id+"F0.wireOp",EDGE,"E47"),sQuery(id+"F0.wireOp",EDGE,"E48"),sQuery(id+"F0.wireOp",EDGE,"E49"),sQuery(id+"F0.wireOp",EDGE,"E50"),sQuery(id+"F0.wireOp",EDGE,"E51"),sQuery(id+"F0.wireOp",EDGE,"E52"),sQuery(id+"F0.wireOp",EDGE,"E53"),sQuery(id+"F0.wireOp",EDGE,"E54"),sQuery(id+"F0.wireOp",EDGE,"E55"),sQuery(id+"F0.wireOp",EDGE,"E56"),sQuery(id+"F0.wireOp",EDGE,"E57"),sQuery(id+"F0.wireOp",EDGE,"E58"),sQuery(id+"F0.wireOp",EDGE,"E59"),sQuery(id+"F0.wireOp",EDGE,"E60"),sQuery(id+"F0.wireOp",EDGE,"E61"),sQuery(id+"F0.wireOp",EDGE,"E62"),sQuery(id+"F0.wireOp",EDGE,"E63"),sQuery(id+"F0.wireOp",EDGE,"E64"),sQuery(id+"F0.wireOp",EDGE,"E65"),sQuery(id+"F0.wireOp",EDGE,"E66"),sQuery(id+"F0.wireOp",EDGE,"E67"),sQuery(id+"F0.wireOp",EDGE,"E68"),sQuery(id+"F0.wireOp",EDGE,"E69"),sQuery(id+"F0.wireOp",EDGE,"E70"),sQuery(id+"F0.wireOp",EDGE,"E71"),sQuery(id+"F0.wireOp",EDGE,"E72"),sQuery(id+"F0.wireOp",EDGE,"E73"),sQuery(id+"F0.wireOp",EDGE,"E74"),sQuery(id+"F0.wireOp",EDGE,"E75"),sQuery(id+"F0.wireOp",EDGE,"E76"),sQuery(id+"F0.wireOp",EDGE,"E77"),sQuery(id+"F0.wireOp",EDGE,"E78"),sQuery(id+"F0.wireOp",EDGE,"E79"),sQuery(id+"F0.wireOp",EDGE,"E80"),sQuery(id+"F0.wireOp",EDGE,"E81"),sQuery(id+"F0.wireOp",EDGE,"E82"),sQuery(id+"F0.wireOp",EDGE,"E83"),sQuery(id+"F0.wireOp",EDGE,"E84"),sQuery(id+"F0.wireOp",EDGE,"E85"),sQuery(id+"F0.wireOp",EDGE,"E86"),sQuery(id+"F0.wireOp",EDGE,"E87"),sQuery(id+"F0.wireOp",EDGE,"E88"),sQuery(id+"F0.wireOp",EDGE,"E89"),sQuery(id+"F0.wireOp",EDGE,"E90"),sQuery(id+"F0.wireOp",EDGE,"E91"),sQuery(id+"F0.wireOp",EDGE,"E92"),sQuery(id+"F0.wireOp",EDGE,"E93"),sQuery(id+"F0.wireOp",EDGE,"E94"),sQuery(id+"F0.wireOp",EDGE,"E95"),sQuery(id+"F0.wireOp",EDGE,"E96"),sQuery(id+"F0.wireOp",EDGE,"E97"),sQuery(id+"F0.wireOp",EDGE,"E98"),sQuery(id+"F0.wireOp",EDGE,"E99"),sQuery(id+"F0.wireOp",EDGE,"E100"),sQuery(id+"F0.wireOp",EDGE,"E101"),sQuery(id+"F0.wireOp",EDGE,"E102"),sQuery(id+"F0.wireOp",EDGE,"E103"),sQuery(id+"F0.wireOp",EDGE,"E173"),sQuery(id+"F0.wireOp",EDGE,"E174"),sQuery(id+"F0.wireOp",EDGE,"E175"),sQuery(id+"F0.wireOp",EDGE,"E180"),sQuery(id+"F0.wireOp",EDGE,"E181"),sQuery(id+"F0.wireOp",EDGE,"E182"),sQuery(id+"F0.wireOp",EDGE,"E183"),sQuery(id+"F0.wireOp",EDGE,"E184"),sQuery(id+"F0.wireOp",EDGE,"E185"),sQuery(id+"F0.wireOp",EDGE,"E186"),sQuery(id+"F0.wireOp",EDGE,"E187"),sQuery(id+"F0.wireOp",EDGE,"E188"),sQuery(id+"F0.wireOp",EDGE,"E189"),sQuery(id+"F0.wireOp",EDGE,"E200"),sQuery(id+"F0.wireOp",EDGE,"E201"),sQuery(id+"F0.wireOp",EDGE,"E202"),sQuery(id+"F0.wireOp",EDGE,"E203"),sQuery(id+"F0.wireOp",EDGE,"E204"),sQuery(id+"F0.wireOp",EDGE,"E205"),sQuery(id+"F0.wireOp",EDGE,"E206"),sQuery(id+"F0.wireOp",EDGE,"E207"),sQuery(id+"F0.wireOp",EDGE,"97428e1f-2df1-4eb4-ba85-a1d425946b56"),sQuery(id+"F0.wireOp",EDGE,"E218"),sQuery(id+"F0.wireOp",EDGE,"E219"),sQuery(id+"F0.wireOp",EDGE,"E220"),sQuery(id+"F0.wireOp",EDGE,"E221"),sQuery(id+"F0.wireOp",EDGE,"E222"),sQuery(id+"F0.wireOp",EDGE,"E223"),sQuery(id+"F0.wireOp",EDGE,"E224"),sQuery(id+"F0.wireOp",EDGE,"E225"),sQuery(id+"F0.wireOp",EDGE,"E226"),sQuery(id+"F0.wireOp",EDGE,"E227"),sQuery(id+"F0.wireOp",EDGE,"E228"),sQuery(id+"F0.wireOp",EDGE,"E229"),sQuery(id+"F0.wireOp",EDGE,"E230"),sQuery(id+"F0.wireOp",EDGE,"E231"),sQuery(id+"F0.wireOp",EDGE,"E232"),sQuery(id+"F0.wireOp",EDGE,"E233"),sQuery(id+"F0.wireOp",EDGE,"E234")])],"isStart":true});
            extrude(context, id + "F3", {"entities" : qUnion([Q0, Q1]), "operationType" : NewBodyOperationType.ADD, "endBound" : BoundingType.UP_TO_SURFACE, "oppositeDirection" : true, "depth" : 25 * mm, "endBoundEntityFace" : qUnion([Q2]), "offsetDistance" : 25 * mm});
        }
        {
            var Q0;
            Q0=makeQuery(id+"F2.imprint","IMPRINT",FACE,{"disambiguationData":[TD([[makeQuery(id+"F2.imprint","IMPRINT",EDGE,{"derivedFrom":sQuery(id+"F2.wireOp",EDGE,"E254")}),1.0]])]});
            var Q1;
            {var subQ0=sQuery(id+"F2.wireOp",EDGE,"E265");var subQ1=sQuery(id+"F2.wireOp",EDGE,"E255");var subQ2=makeQuery(id+"F2.imprint","INTERSECT",VERTEX,{"disambiguationData":[OD(0.0)],"derivedFrom":[subQ1,subQ0]});Q1=makeQuery(id+"F2.imprint","IMPRINT",FACE,{"disambiguationData":[TD([[makeQuery(id+"F2.imprint","IMPRINT",EDGE,{"disambiguationData":[TD([[subQ2,1.0]])],"derivedFrom":subQ1}),1.0]])]});}
            var Q2;
            {var subQ0=sQuery(id+"F2.wireOp",EDGE,"E265");var subQ1=sQuery(id+"F2.wireOp",EDGE,"E260.MirrorC");var subQ2=makeQuery(id+"F2.imprint","INTERSECT",VERTEX,{"disambiguationData":[OD(0.0)],"derivedFrom":[subQ1,subQ0]});Q2=makeQuery(id+"F2.imprint","IMPRINT",FACE,{"disambiguationData":[TD([[makeQuery(id+"F2.imprint","IMPRINT",EDGE,{"disambiguationData":[TD([[subQ2,-1.0]])],"derivedFrom":subQ1}),-1.0]])]});}
            var Q3;
            Q3=makeQuery(id+"F2.imprint","IMPRINT",FACE,{"disambiguationData":[TD([[makeQuery(id+"F2.imprint","IMPRINT",EDGE,{"derivedFrom":sQuery(id+"F2.wireOp",EDGE,"E259.MirrorC")}),-1.0]])]});
            var Q4;
            Q4=makeQuery(id+"F2.imprint","IMPRINT",FACE,{"disambiguationData":[TD([[makeQuery(id+"F2.imprint","IMPRINT",EDGE,{"derivedFrom":sQuery(id+"F2.wireOp",EDGE,"E257.MirrorC")}),-1.0]])]});
            var Q5;
            {var subQ0=sQuery(id+"F2.wireOp",EDGE,"E270.MirrorCS");var subQ1=sQuery(id+"F2.wireOp",EDGE,"E258.MirrorC");var subQ2=makeQuery(id+"F2.imprint","INTERSECT",VERTEX,{"disambiguationData":[OD(0.0)],"derivedFrom":[subQ1,subQ0]});Q5=makeQuery(id+"F2.imprint","IMPRINT",FACE,{"disambiguationData":[TD([[makeQuery(id+"F2.imprint","IMPRINT",EDGE,{"disambiguationData":[TD([[subQ2,1.0]])],"derivedFrom":subQ1}),-1.0]])]});}
            var Q6;
            {var subQ0=sQuery(id+"F2.wireOp",EDGE,"E270.MirrorCS");var subQ1=sQuery(id+"F2.wireOp",EDGE,"E262.MirrorC");var subQ2=makeQuery(id+"F2.imprint","INTERSECT",VERTEX,{"disambiguationData":[OD(0.0)],"derivedFrom":[subQ1,subQ0]});Q6=makeQuery(id+"F2.imprint","IMPRINT",FACE,{"disambiguationData":[TD([[makeQuery(id+"F2.imprint","IMPRINT",EDGE,{"disambiguationData":[TD([[subQ2,-1.0]])],"derivedFrom":subQ1}),1.0]])]});}
            var Q7;
            Q7=makeQuery(id+"F2.imprint","IMPRINT",FACE,{"disambiguationData":[TD([[makeQuery(id+"F2.imprint","IMPRINT",EDGE,{"derivedFrom":sQuery(id+"F2.wireOp",EDGE,"E261.MirrorC")}),1.0]])]});
            var Q8;
            Q8=makeQuery(id+"F2.imprint","IMPRINT",FACE,{"disambiguationData":[TD([[makeQuery(id+"F2.imprint","IMPRINT",EDGE,{"derivedFrom":sQuery(id+"F2.wireOp",EDGE,"E278")}),1.0]])]});
            var Q9;
            Q9=makeQuery(id+"F2.imprint","IMPRINT",FACE,{"disambiguationData":[TD([[makeQuery(id+"F2.imprint","IMPRINT",EDGE,{"derivedFrom":sQuery(id+"F2.wireOp",EDGE,"E279")}),1.0]])]});
            var Q10;
            {var subQ0=sQuery(id+"F0.wireOp",EDGE,"E234");var subQ1=sQuery(id+"F0.wireOp",EDGE,"E233");var subQ2=sQuery(id+"F0.wireOp",EDGE,"E232");var subQ3=sQuery(id+"F0.wireOp",EDGE,"E231");var subQ4=sQuery(id+"F0.wireOp",EDGE,"E230");var subQ5=sQuery(id+"F0.wireOp",EDGE,"E229");var subQ6=sQuery(id+"F0.wireOp",EDGE,"E228");var subQ7=sQuery(id+"F0.wireOp",EDGE,"E227");var subQ8=sQuery(id+"F0.wireOp",EDGE,"E226");var subQ9=sQuery(id+"F0.wireOp",EDGE,"E225");var subQ10=sQuery(id+"F0.wireOp",EDGE,"E224");var subQ11=sQuery(id+"F0.wireOp",EDGE,"E223");var subQ12=sQuery(id+"F0.wireOp",EDGE,"E222");var subQ13=sQuery(id+"F0.wireOp",EDGE,"E221");var subQ14=sQuery(id+"F0.wireOp",EDGE,"E220");var subQ15=sQuery(id+"F0.wireOp",EDGE,"E219");var subQ16=sQuery(id+"F0.wireOp",EDGE,"E218");var subQ17=sQuery(id+"F0.wireOp",EDGE,"97428e1f-2df1-4eb4-ba85-a1d425946b56");var subQ18=sQuery(id+"F0.wireOp",EDGE,"E207");var subQ19=sQuery(id+"F0.wireOp",EDGE,"E206");var subQ20=sQuery(id+"F0.wireOp",EDGE,"E205");var subQ21=sQuery(id+"F0.wireOp",EDGE,"E204");var subQ22=sQuery(id+"F0.wireOp",EDGE,"E203");var subQ23=sQuery(id+"F0.wireOp",EDGE,"E202");var subQ24=sQuery(id+"F0.wireOp",EDGE,"E201");var subQ25=sQuery(id+"F0.wireOp",EDGE,"E200");var subQ26=sQuery(id+"F0.wireOp",EDGE,"E189");var subQ27=sQuery(id+"F0.wireOp",EDGE,"E188");var subQ28=sQuery(id+"F0.wireOp",EDGE,"E187");var subQ29=sQuery(id+"F0.wireOp",EDGE,"E186");var subQ30=sQuery(id+"F0.wireOp",EDGE,"E185");var subQ31=sQuery(id+"F0.wireOp",EDGE,"E184");var subQ32=sQuery(id+"F0.wireOp",EDGE,"E183");var subQ33=sQuery(id+"F0.wireOp",EDGE,"E182");var subQ34=sQuery(id+"F0.wireOp",EDGE,"E181");var subQ35=sQuery(id+"F0.wireOp",EDGE,"E180");var subQ36=sQuery(id+"F0.wireOp",EDGE,"E175");var subQ37=sQuery(id+"F0.wireOp",EDGE,"E174");var subQ38=sQuery(id+"F0.wireOp",EDGE,"E173");var subQ39=sQuery(id+"F0.wireOp",EDGE,"E103");var subQ40=sQuery(id+"F0.wireOp",EDGE,"E102");var subQ41=sQuery(id+"F0.wireOp",EDGE,"E101");var subQ42=sQuery(id+"F0.wireOp",EDGE,"E100");var subQ43=sQuery(id+"F0.wireOp",EDGE,"E99");var subQ44=sQuery(id+"F0.wireOp",EDGE,"E98");var subQ45=sQuery(id+"F0.wireOp",EDGE,"E97");var subQ46=sQuery(id+"F0.wireOp",EDGE,"E96");var subQ47=sQuery(id+"F0.wireOp",EDGE,"E95");var subQ48=sQuery(id+"F0.wireOp",EDGE,"E94");var subQ49=sQuery(id+"F0.wireOp",EDGE,"E93");var subQ50=sQuery(id+"F0.wireOp",EDGE,"E92");var subQ51=sQuery(id+"F0.wireOp",EDGE,"E91");var subQ52=sQuery(id+"F0.wireOp",EDGE,"E90");var subQ53=sQuery(id+"F0.wireOp",EDGE,"E89");var subQ54=sQuery(id+"F0.wireOp",EDGE,"E88");var subQ55=sQuery(id+"F0.wireOp",EDGE,"E87");var subQ56=sQuery(id+"F0.wireOp",EDGE,"E86");var subQ57=sQuery(id+"F0.wireOp",EDGE,"E85");var subQ58=sQuery(id+"F0.wireOp",EDGE,"E84");var subQ59=sQuery(id+"F0.wireOp",EDGE,"E83");var subQ60=sQuery(id+"F0.wireOp",EDGE,"E82");var subQ61=sQuery(id+"F0.wireOp",EDGE,"E81");var subQ62=sQuery(id+"F0.wireOp",EDGE,"E80");var subQ63=sQuery(id+"F0.wireOp",EDGE,"E79");var subQ64=sQuery(id+"F0.wireOp",EDGE,"E78");var subQ65=sQuery(id+"F0.wireOp",EDGE,"E77");var subQ66=sQuery(id+"F0.wireOp",EDGE,"E76");var subQ67=sQuery(id+"F0.wireOp",EDGE,"E75");var subQ68=sQuery(id+"F0.wireOp",EDGE,"E74");var subQ69=sQuery(id+"F0.wireOp",EDGE,"E73");var subQ70=sQuery(id+"F0.wireOp",EDGE,"E72");var subQ71=sQuery(id+"F0.wireOp",EDGE,"E71");var subQ72=sQuery(id+"F0.wireOp",EDGE,"E70");var subQ73=sQuery(id+"F0.wireOp",EDGE,"E69");var subQ74=sQuery(id+"F0.wireOp",EDGE,"E68");var subQ75=sQuery(id+"F0.wireOp",EDGE,"E67");var subQ76=sQuery(id+"F0.wireOp",EDGE,"E66");var subQ77=sQuery(id+"F0.wireOp",EDGE,"E65");var subQ78=sQuery(id+"F0.wireOp",EDGE,"E64");var subQ79=sQuery(id+"F0.wireOp",EDGE,"E63");var subQ80=sQuery(id+"F0.wireOp",EDGE,"E62");var subQ81=sQuery(id+"F0.wireOp",EDGE,"E61");var subQ82=sQuery(id+"F0.wireOp",EDGE,"E60");var subQ83=sQuery(id+"F0.wireOp",EDGE,"E59");var subQ84=sQuery(id+"F0.wireOp",EDGE,"E58");var subQ85=sQuery(id+"F0.wireOp",EDGE,"E57");var subQ86=sQuery(id+"F0.wireOp",EDGE,"E56");var subQ87=sQuery(id+"F0.wireOp",EDGE,"E55");var subQ88=sQuery(id+"F0.wireOp",EDGE,"E54");var subQ89=sQuery(id+"F0.wireOp",EDGE,"E53");var subQ90=sQuery(id+"F0.wireOp",EDGE,"E52");var subQ91=sQuery(id+"F0.wireOp",EDGE,"E51");var subQ92=sQuery(id+"F0.wireOp",EDGE,"E50");var subQ93=sQuery(id+"F0.wireOp",EDGE,"E49");var subQ94=sQuery(id+"F0.wireOp",EDGE,"E48");var subQ95=sQuery(id+"F0.wireOp",EDGE,"E47");var subQ96=sQuery(id+"F0.wireOp",EDGE,"E46");var subQ97=sQuery(id+"F0.wireOp",EDGE,"E45");var subQ98=sQuery(id+"F0.wireOp",EDGE,"E44");var subQ99=sQuery(id+"F0.wireOp",EDGE,"E43");var subQ100=sQuery(id+"F0.wireOp",EDGE,"E42");var subQ101=sQuery(id+"F0.wireOp",EDGE,"E41");var subQ102=sQuery(id+"F0.wireOp",EDGE,"E40");var subQ103=sQuery(id+"F0.wireOp",EDGE,"E39");var subQ104=sQuery(id+"F0.wireOp",EDGE,"E38");var subQ105=sQuery(id+"F0.wireOp",EDGE,"E37");var subQ106=sQuery(id+"F0.wireOp",EDGE,"E36");Q10=makeQuery(id+"F3.boolean.opBoolean","MERGE",FACE,{"derivedFrom":[makeQuery(id+"F1.opExtrude","CAP_FACE",FACE,{"disambiguationData":[OSD([subQ106,subQ105,subQ104,subQ103,subQ102,subQ101,subQ100,subQ99,subQ98,subQ97,subQ96,subQ95,subQ94,subQ93,subQ92,subQ91,subQ90,subQ89,subQ88,subQ87,subQ86,subQ85,subQ84,subQ83,subQ82,subQ81,subQ80,subQ79,subQ78,subQ77,subQ76,subQ75,subQ74,subQ73,subQ72,subQ71,subQ70,subQ69,subQ68,subQ67,subQ66,subQ65,subQ64,subQ63,subQ62,subQ61,subQ60,subQ59,subQ58,subQ57,subQ56,subQ55,subQ54,subQ53,subQ52,subQ51,subQ50,subQ49,subQ48,subQ47,subQ46,subQ45,subQ44,subQ43,subQ42,subQ41,subQ40,subQ39,subQ38,subQ37,subQ36,subQ35,subQ34,subQ33,subQ32,subQ31,subQ30,subQ29,subQ28,subQ27,subQ26,subQ25,subQ24,subQ23,subQ22,subQ21,subQ20,subQ19,subQ18,subQ17,subQ16,subQ15,subQ14,subQ13,subQ12,subQ11,subQ10,subQ9,subQ8,subQ7,subQ6,subQ5,subQ4,subQ3,subQ2,subQ1,subQ0])],"isStart":true}),makeQuery(id+"F3.opExtrude","CAP_FACE",FACE,{"disambiguationData":[OSD([subQ106,subQ105,subQ104,subQ103,subQ102,subQ101,subQ100,subQ99,subQ98,subQ97,subQ96,subQ95,subQ94,subQ93,subQ92,subQ91,subQ90,subQ89,subQ88,subQ87,subQ86,subQ85,subQ84,subQ83,subQ82,subQ81,subQ80,subQ79,subQ78,subQ77,subQ76,subQ75,subQ74,subQ73,subQ72,subQ71,subQ70,subQ69,subQ68,subQ67,subQ66,subQ65,subQ64,subQ63,subQ62,subQ61,subQ60,subQ59,subQ58,subQ57,subQ56,subQ55,subQ54,subQ53,subQ52,subQ51,subQ50,subQ49,subQ48,subQ47,subQ46,subQ45,subQ44,subQ43,subQ42,subQ41,subQ40,subQ39,subQ38,subQ37,subQ36,subQ35,subQ34,subQ33,subQ32,subQ31,subQ30,subQ29,subQ28,subQ27,subQ26,subQ25,subQ24,subQ23,subQ22,subQ21,subQ20,subQ19,subQ18,subQ17,subQ16,subQ15,subQ14,subQ13,subQ12,subQ11,subQ10,subQ9,subQ8,subQ7,subQ6,subQ5,subQ4,subQ3,subQ2,subQ1,subQ0]),OD(0.0)],"isStart":false}),makeQuery(id+"F3.opExtrude","CAP_FACE",FACE,{"disambiguationData":[OSD([subQ106,subQ105,subQ104,subQ103,subQ102,subQ101,subQ100,subQ99,subQ98,subQ97,subQ96,subQ95,subQ94,subQ93,subQ92,subQ91,subQ90,subQ89,subQ88,subQ87,subQ86,subQ85,subQ84,subQ83,subQ82,subQ81,subQ80,subQ79,subQ78,subQ77,subQ76,subQ75,subQ74,subQ73,subQ72,subQ71,subQ70,subQ69,subQ68,subQ67,subQ66,subQ65,subQ64,subQ63,subQ62,subQ61,subQ60,subQ59,subQ58,subQ57,subQ56,subQ55,subQ54,subQ53,subQ52,subQ51,subQ50,subQ49,subQ48,subQ47,subQ46,subQ45,subQ44,subQ43,subQ42,subQ41,subQ40,subQ39,subQ38,subQ37,subQ36,subQ35,subQ34,subQ33,subQ32,subQ31,subQ30,subQ29,subQ28,subQ27,subQ26,subQ25,subQ24,subQ23,subQ22,subQ21,subQ20,subQ19,subQ18,subQ17,subQ16,subQ15,subQ14,subQ13,subQ12,subQ11,subQ10,subQ9,subQ8,subQ7,subQ6,subQ5,subQ4,subQ3,subQ2,subQ1,subQ0]),OD(1.0)],"isStart":false})]});}
            extrude(context, id + "F4", {"entities" : qUnion([Q0, Q1, Q2, Q3, Q4, Q5, Q6, Q7, Q8, Q9]), "operationType" : NewBodyOperationType.REMOVE, "endBound" : BoundingType.UP_TO_SURFACE, "oppositeDirection" : true, "depth" : 25 * mm, "endBoundEntityFace" : qUnion([Q10]), "offsetDistance" : 25 * mm});
        }
    });
